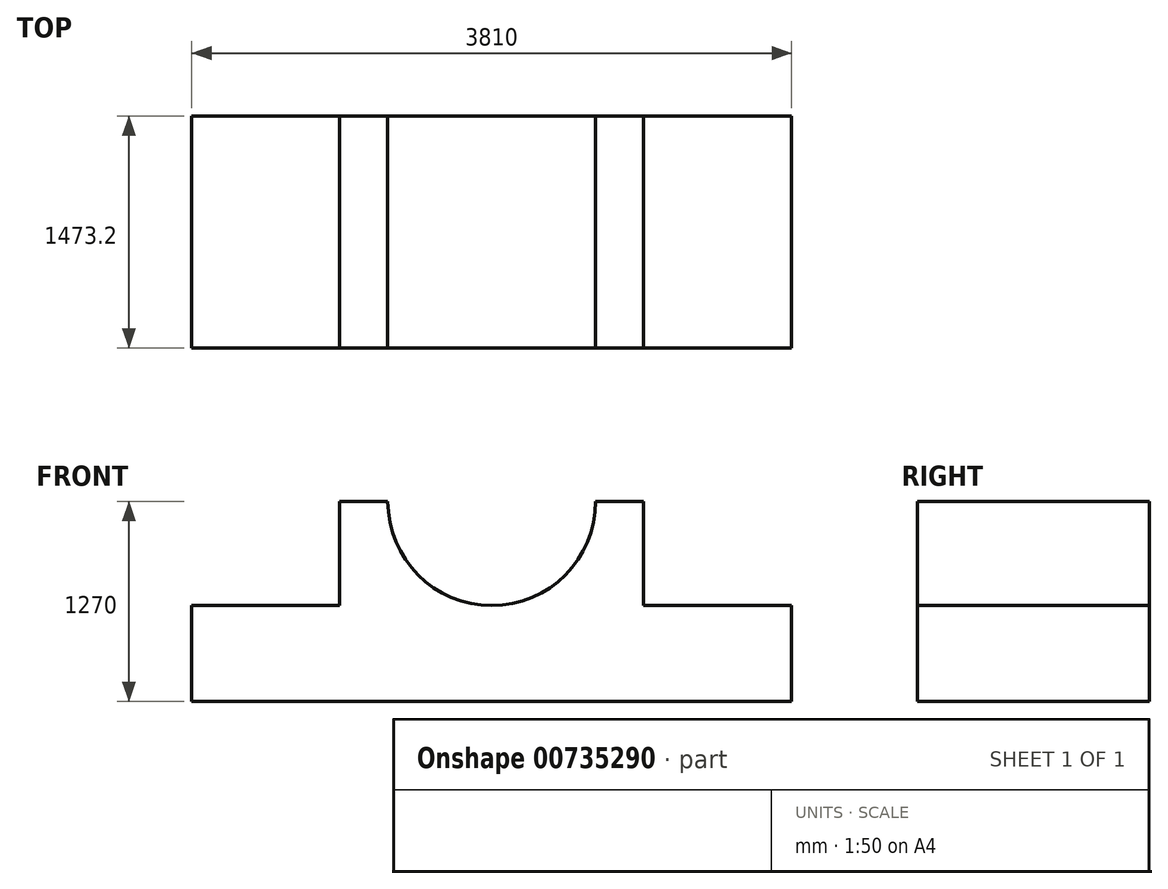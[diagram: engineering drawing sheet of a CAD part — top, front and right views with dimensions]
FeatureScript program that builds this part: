
annotation { "Feature Type Name" : "Feature", "Feature Type Description" : "" }
export const myFeature = defineFeature(function(context is Context, id is Id, definition is map)
    precondition{}
    {
        {
            var Q0;
            Q0=qCreatedBy(makeId("Front.planeOp"),FACE);
            var sketch = newSketch(context, id + "F0", { "sketchPlane" : qUnion([Q0])});
            skLineSegment(sketch, "E0", {"start": v(-939.8, -243.03) * mm, "end": v(2870.2, -243.03) * mm});
            skLineSegment(sketch, "E1", {"start": v(-939.8, 366.57) * mm, "end": v(0, 366.57) * mm});
            skArc(sketch, "E2", {"start": v(1625.6, 1026.97) * mm, "mid": v(1626.6, 1047.99) * mm, "end": v(1626.94, 1069.02) * mm});
            skLineSegment(sketch, "E3", {"start": v(-939.8, 366.57) * mm, "end": v(-939.8, -243.03) * mm});
            skLineSegment(sketch, "E4", {"start": v(2870.2, -243.03) * mm, "end": v(2870.2, 366.57) * mm});
            skPoint(sketch, "E5.end.orphan", {"position": v(1626.94, 1069.02) * mm});
            skLineSegment(sketch, "E6", {"start": v(2870.2, 366.57) * mm, "end": v(1930.4, 366.57) * mm});
            skLineSegment(sketch, "E7", {"start": v(1930.4, 366.57) * mm, "end": v(1930.4, 1026.97) * mm});
            skLineSegment(sketch, "E8", {"start": v(1930.4, 1026.97) * mm, "end": v(1625.6, 1026.97) * mm});
            skLineSegment(sketch, "E9", {"start": v(0, 366.57) * mm, "end": v(0, 1026.97) * mm});
            skLineSegment(sketch, "E10", {"start": v(0, 1026.97) * mm, "end": v(304.8, 1026.97) * mm});
            skCircle(sketch, "E11", {"center": v(965.2, 1026.97) * mm, "radius": 660.4 * mm});
            skSolve(sketch);
        }
        {
            var Q0;
            Q0=makeQuery(id+"F0.imprint","IMPRINT",FACE,{"disambiguationData":[TD([[makeQuery(id+"F0.imprint","IMPRINT",EDGE,{"derivedFrom":sQuery(id+"F0.wireOp",EDGE,"E0")}),1.0]])]});
            extrude(context, id + "F1", {"entities" : qUnion([Q0]), "depth" : 1473.2 * mm, "offsetDistance" : 25.4 * mm});
        }
    });
